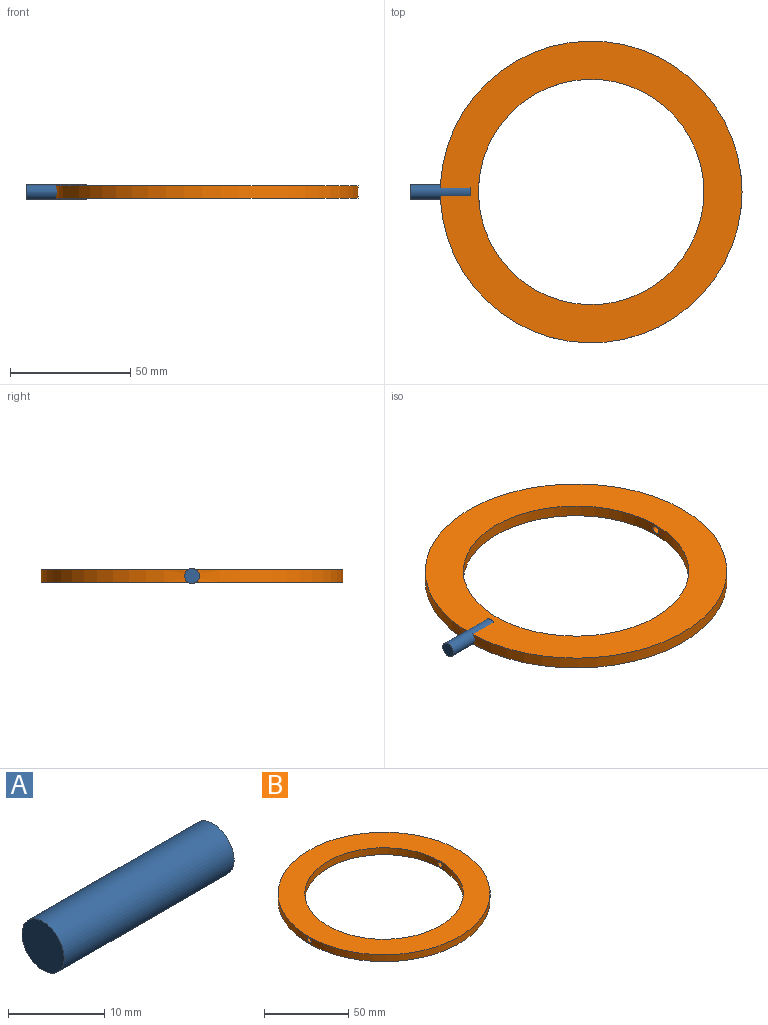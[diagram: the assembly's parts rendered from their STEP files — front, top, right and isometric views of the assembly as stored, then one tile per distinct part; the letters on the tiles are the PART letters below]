
ASSEMBLY  parts=2 mates=1
PART A: 3 faces, bbox 25x6.2x6.2 mm
  f0: cylinder r=3.1mm len=25mm, axis (-1,0,0), area 486.8mm2, adj f1,f2
  f1: plane 6.2x6.2mm, normal (1,0,0), area 30.2mm2, adj f0
  f2: plane 6.2x6.2mm, normal (-1,0,0), area 30.2mm2, adj f0
PART B: 6 faces, bbox 125.6x125.6x5 mm
  f0: cylinder r=46.94mm len=93.88mm, axis (0,0,-1), area 1455.4mm2, adj f2,f3,f4,f5
  f1: cylinder r=62.82mm len=125.65mm, axis (0,0,-1), area 1954.4mm2, adj f2,f3,f4,f5
  f2: plane 125.65x125.65mm, normal (0,0,1), area 5477.1mm2, adj f0,f1
  f3: plane 125.65x125.65mm, normal (0,0,-1), area 5477.1mm2, adj f0,f1
  f4: cylinder r=1.75mm len=15.92mm, axis (1,0,0), area 174.7mm2, adj f0,f1
  f5: cylinder r=1.75mm len=15.92mm, axis (1,0,0), area 174.7mm2, adj f0,f1
PLACE A t=(-126.99,-13.93,79.2)mm
PLACE B t=(-51.57,-13.93,26.82)mm
MATE cylindrical A.f0 <-> B.f4  axis (-1,0,0) through (-114.49,-13.93,29.32)mm
